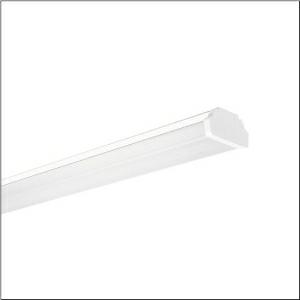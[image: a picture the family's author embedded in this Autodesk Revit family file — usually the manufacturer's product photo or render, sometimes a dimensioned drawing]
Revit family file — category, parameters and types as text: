
# Revit family: dus_31_gen_2_53bd812dv4d5d2_2233
name_source: partatom
category: Lighting Fixtures
units: mm (PartAtom-declared; Revit-internal decimal feet)

## family parameters
Cut with Voids When Loaded = No
Host = Face
Light Source = No
Part Type = Normal
Room Calculation Point = No
Round Connector Dimension = Use Diameter
Shared = No

## types (1)
- --- (1 x LED, 13680 lm, 74.9 W, 4000K)
    Apparent Load = 75 VA
    CIE Flux Codes = 47 80 95 93 100
    Color Rendering = 80
    Color Temperature = 4000K
    Default Elevation = 1800 mm
    Description = DUS 31 Gen.2, luminaire insert, of sheet steel, coil coated, white, length: 1.535mm, width: 81mm, height: 90mm, 5x system unit, system units: 307mm, LED rated luminous flux: 13.680lm, light colour: 840, SDCM (Standard Deviation of Colour Matching)MacAdam ≤ 3 SDCM (initial), control gear: DALI 2, control gear: ECG DALI, with plug, 5-pole, with phase selection, mains connection: 220..240V, AC, 50/60Hz, rated input power: 75W, through-wiring accessed according to module size, primary optical cover: cover, of PMMA, light emission: direct distribution, primary light characteristic: symmetric, protection rating (complete): IP20, protection rating (LED compartment): IP50, insulation class (complete): insulation class I (protective earthing), certification: CE, ENEC, VDE, UKCA, impact resistance: IK03, permissible ambient temperature for indoor applications: -25..+35°C, corresponds to IFS (International Featured Standards) requirements for safety and quality in the food industry, reducing of maximum allowable ambient temperature of 5°C with ceiling mounting, packaging unit: 1 piece
    Height = 95 mm
    Lamp = 1 x LED
    Lamp Light Flux = 13680 lm
    Lamp Power = 74.9 W
    Lamp count = 1
    Length = 1535 mm
    Luminous efficacy = 183 lm/W
    Manufacturer = Siteco
    ModVariant = No
    Model = 53BD812DV4D5D2
    Mounting Place = Ceiling
    Mounting Type = Pendant
    Number of Poles = 1
    OnlyDefault = Yes
    Power Factor = 1
    Product Name = DUS 31 Gen.2
    Product group = luminaire insert | ceiling pendant
    ProductGroupID = 901
    Protection Class = Protection class I
    Protection Degree = IP 20
    RLX_Detail_Level = 1
    RLX_Emergency_Light_Flux = 0 lm
    RLX_Emergency_Type = 0
    RLX_Emergency_Type_DB = No
    RlxData = <blob elided: 32205 chars, md5=df45b9c2>
    Socket = socket
    Standby Power = 0 W
    System Light Flux = 13680 lm
    System Power = 75 W
    Type Comments = factory setting: luminous flux: 100 % | dim-lin: 254 | 511 mA
    Type Image = l_1319596.jpg
    URL = http://relux.com
    VarID = @adj_049785
    Voltage = 0 V
    Weight = 0.00 kg
    Width = 81 mm

## geometry (parser evidence)
native form markers: Blend x4, Sweep x13
no freeform markers — native parametric forms only
